# Revit family: MFZ-KT35VG-E1(ET1)
name_source: partatom
category: Mechanical Equipment
revit_build: Autodesk Revit 2016 (Build: 20150714_1515(x64)
units: mm (PartAtom-declared; Revit-internal decimal feet)

## family parameters
Always vertical = Yes
Cut with Voids When Loaded = No
OmniClass Number = 23.75.00.00
OmniClass Title = Climate Control (HVAC)
Part Type = Normal
Room Calculation Point = No
Round Connector Dimension = Use Radius
Shared = No
Work Plane-Based = No

## types (1)
- MFZ-KT35VG-E1 (ET1)
    Air Direction = 4
    Cooling Air Flow 1_High (m3/h) = 468
    Cooling Air Flow 1_Low (m3/h) = 288
    Cooling Air Flow 1_Med. (m3/h) = 390
    Cooling Air Flow 1_Silent (m3/h) = 234
    Cooling Air Flow 1_Super High (m3/h) = 534
    Cooling Air Flow 2_High (m3/h) = 468
    Cooling Air Flow 2_Low (m3/h) = 288
    Cooling Air Flow 2_Med. (m3/h) = 390
    Cooling Air Flow 2_Silent (m3/h) = 252
    Cooling Air Flow 2_Super High (m3/h) = 540
    Cooling Fan Motor Current (A) = 0.14
    Cooling Fan Speed 1_High (rpm) = 900
    Cooling Fan Speed 1_Low (rpm) = 610
    Cooling Fan Speed 1_Med. (rpm) = 770
    Cooling Fan Speed 1_Silent (rpm) = 520
    Cooling Fan Speed 1_Super High (rpm) = 1000
    Cooling Fan Speed 2_High (rpm) = 900
    Cooling Fan Speed 2_Low (rpm) = 610
    Cooling Fan Speed 2_Med. (rpm) = 770
    Cooling Fan Speed 2_Silent (rpm) = 550
    Cooling Fan Speed 2_Super High (rpm) = 1010
    Cooling Power Input (W) = 20 W
    Cooling Running Current (A) = 0.17
    Cooling Sound Level 1_High (db(A)) = 37
    Cooling Sound Level 1_Low (db(A)) = 24
    Cooling Sound Level 1_Med. (db(A)) = 31
    Cooling Sound Level 1_Silent (db(A)) = 19
    Cooling Sound Level 1_Super High (db(A)) = 41
    Cooling Sound Level 2_High (db(A)) = 38
    Cooling Sound Level 2_Low (db(A)) = 28
    Cooling Sound Level 2_Med. (db(A)) = 33
    Cooling Sound Level 2_Silent (db(A)) = 23
    Cooling Sound Level 2_Super High (db(A)) = 43
    Depth (mm) = 215 mm
    Drain pipe_radius (mm) = 8 mm  [stored 0.0262467 ft]
    Fan Motor Model = RC0J30-Q#
    Fan Speed Regulator = 5
    Gas pipe_radius (mm) = 4.76 mm
    Heating Air Flow 1_High (m3/h) = 438
    Heating Air Flow 1_Low (m3/h) = 240
    Heating Air Flow 1_Med. (m3/h) = 336
    Heating Air Flow 1_Silent (m3/h) = 210
    Heating Air Flow 1_Super High (m3/h) = 582
    Heating Air Flow 2_High (m3/h) = 468
    Heating Air Flow 2_Low (m3/h) = 294
    Heating Air Flow 2_Med. (m3/h) = 378
    Heating Air Flow 2_Silent (m3/h) = 252
    Heating Air Flow 2_Super High (m3/h) = 582
    Heating Fan Motor Current (A) = 0.17
    Heating Fan Speed 1_High (rpm) = 850
    Heating Fan Speed 1_Low (rpm) = 530
    Heating Fan Speed 1_Med. (rpm) = 690
    Heating Fan Speed 1_Silent (rpm) = 480
    Heating Fan Speed 1_Super High (rpm) = 1080
    Heating Fan Speed 2_High (rpm) = 900
    Heating Fan Speed 2_Low (rpm) = 620
    Heating Fan Speed 2_Med. (rpm) = 750
    Heating Fan Speed 2_Silent (rpm) = 550
    Heating Fan Speed 2_Super High (rpm) = 1080
    Heating Power Input (W) = 24 W
    Heating Running Current (A) = 0.2
    Heating Sound Level 1_Hgh (db(A)) = 37
    Heating Sound Level 1_Low (db(A)) = 23
    Heating Sound Level 1_Med. (db(A)) = 30
    Heating Sound Level 1_Silent (dB(A)) = 19
    Heating Sound Level 1_Super Hgh (db(A)) = 44
    Heating Sound Level 2_Hgh (db(A)) = 39
    Heating Sound Level 2_Low (db(A)) = 28
    Heating Sound Level 2_Med. (db(A)) = 34
    Heating Sound Level 2_Silent (dB(A)) = 24
    Heating Sound Level 2_Super Hgh (db(A)) = 44
    Height (mm) = 600 mm
    Hertz = 50 Hz
    Liquid pipe_radius (mm) = 3.175 mm  [stored 0.0104167 ft]
    Manufacturer = Mitsubishi Electric Corporation
    Model = MFZ-KT35VG
    Phase = 1
    Remote Controller Model = SG191
    Space View = Yes
    Subcategory = HVAC
    URL = http://www.mitsubishielectric.com
    Unit Weight (kg) = 14.5
    Voltage = 230 V
    Width (mm) = 750 mm  [stored 2.46063 ft]

note: [stored X ft] marks values corroborated as IEEE doubles in the binary element streams (Revit-internal decimal feet)

## geometry (parser evidence)
native form markers: Blend x40, Sweep x2
no freeform markers — native parametric forms only
